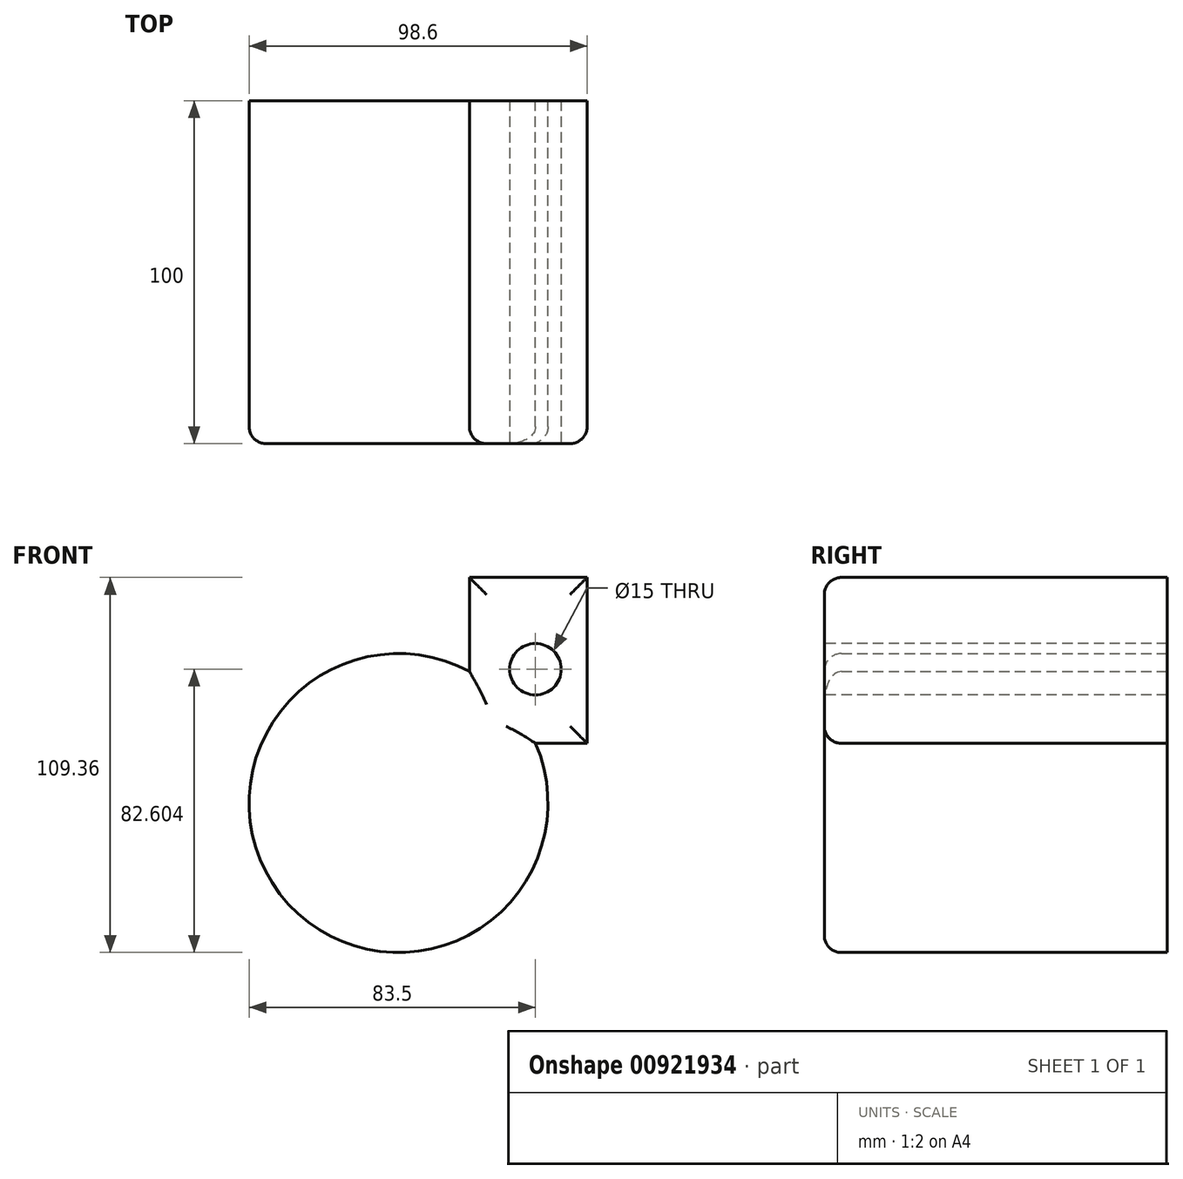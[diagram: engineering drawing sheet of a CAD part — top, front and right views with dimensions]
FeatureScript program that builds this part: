
annotation { "Feature Type Name" : "Feature", "Feature Type Description" : "" }
export const myFeature = defineFeature(function(context is Context, id is Id, definition is map)
    precondition{}
    {
        {
            var Q0;
            Q0=qCreatedBy(makeId("Front.planeOp"),FACE);
            var sketch = newSketch(context, id + "F0", { "sketchPlane" : qUnion([Q0])});
            skCircle(sketch, "E0", {"center": v(0, 0) * mm, "radius": 43.58 * mm});
            skLineSegment(sketch, "E1.bottom", {"start": v(20.68, 17.41) * mm, "end": v(55.02, 17.41) * mm});
            skLineSegment(sketch, "E1.top", {"start": v(20.68, 65.78) * mm, "end": v(55.02, 65.78) * mm});
            skLineSegment(sketch, "E1.left", {"start": v(20.68, 17.41) * mm, "end": v(20.68, 65.78) * mm});
            skLineSegment(sketch, "E1.right", {"start": v(55.02, 17.41) * mm, "end": v(55.02, 65.78) * mm});
            skSolve(sketch);
        }
        {
            var Q0;
            Q0 = qSketchRegion(id + "F0", true);
            extrude(context, id + "F1", {"entities" : qUnion([Q0]), "endBound" : BoundingType.SYMMETRIC, "depth" : 100 * mm, "offsetDistance" : 25 * mm});
        }
        {
            var Q0;
            Q0=makeQuery(id+"F1.opExtrude","CAP_FACE",FACE,{"disambiguationData":[OSD([sQuery(id+"F0.wireOp",EDGE,"E0"),sQuery(id+"F0.wireOp",EDGE,"E1.bottom"),sQuery(id+"F0.wireOp",EDGE,"E1.top"),sQuery(id+"F0.wireOp",EDGE,"E1.left"),sQuery(id+"F0.wireOp",EDGE,"E1.right")])],"isStart":false});
            var sketch = newSketch(context, id + "F2", { "sketchPlane" : qUnion([Q0])});
            skPoint(sketch, "E2", {"position": v(39.92, 39.02) * mm});
            skSolve(sketch);
        }
        {
            var Q0;
            Q0=sQuery(id+"F2.wireOp",VERTEX,"E2");
            var Q1;
            Q1=makeQuery(id+"F1.opExtrude","SWEPT_BODY",BODY,{"disambiguationData":[OSD([sQuery(id+"F0.wireOp",EDGE,"E0"),sQuery(id+"F0.wireOp",EDGE,"E1.bottom"),sQuery(id+"F0.wireOp",EDGE,"E1.top"),sQuery(id+"F0.wireOp",EDGE,"E1.left"),sQuery(id+"F0.wireOp",EDGE,"E1.right")])]});
            hole(context, id + "F3", {"style" : HoleStyle.SIMPLE, "endStyle" : HoleEndStyle.THROUGH, "holeDiameter" : 15 * mm, "majorDiameter" : 5 * mm, "isTappedThrough" : true, "tappedDepth" : 12 * mm, "tapClearance" : 3, "locations" : qUnion([Q0]), "scope" : qUnion([Q1])});
        }
        {
            var Q0;
            Q0=makeQuery(id+"F1.opExtrude","CAP_EDGE",EDGE,{"disambiguationData":[OSD([sQuery(id+"F0.wireOp",EDGE,"E0")])],"isStart":false});
            var Q1;
            Q1=makeQuery(id+"F1.opExtrude","CAP_EDGE",EDGE,{"disambiguationData":[OSD([sQuery(id+"F0.wireOp",EDGE,"E1.left")])],"isStart":false});
            var Q2;
            Q2=makeQuery(id+"F1.opExtrude","CAP_EDGE",EDGE,{"disambiguationData":[OSD([sQuery(id+"F0.wireOp",EDGE,"E1.top")])],"isStart":false});
            var Q3;
            Q3=makeQuery(id+"F1.opExtrude","CAP_EDGE",EDGE,{"disambiguationData":[OSD([sQuery(id+"F0.wireOp",EDGE,"E1.right")])],"isStart":false});
            var Q4;
            Q4=makeQuery(id+"F1.opExtrude","CAP_EDGE",EDGE,{"disambiguationData":[OSD([sQuery(id+"F0.wireOp",EDGE,"E1.bottom")])],"isStart":false});
            fillet(context, id + "F4", {"entities" : qUnion([Q0, Q1, Q2, Q3, Q4]), "radius" : 5 * mm, "tangentPropagation" : true, "allowEdgeOverflow" : false});
        }
    });
